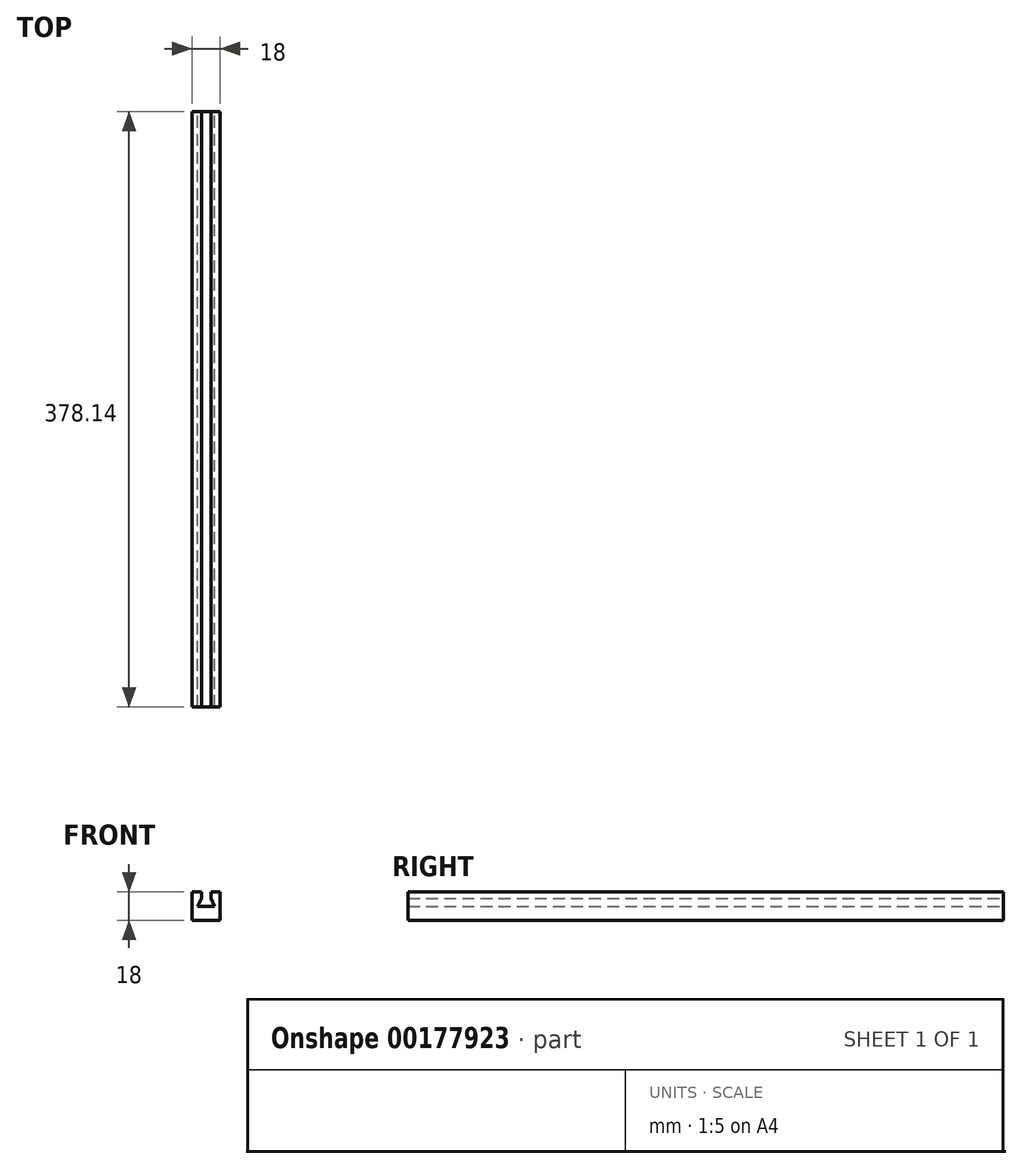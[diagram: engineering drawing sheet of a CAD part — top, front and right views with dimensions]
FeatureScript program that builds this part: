
annotation { "Feature Type Name" : "Feature", "Feature Type Description" : "" }
export const myFeature = defineFeature(function(context is Context, id is Id, definition is map)
    precondition{}
    {
        {
            var Q0;
            Q0=qCreatedBy(makeId("Front.planeOp"),FACE);
            var sketch = newSketch(context, id + "F0", { "sketchPlane" : qUnion([Q0])});
            skLineSegment(sketch, "E0.trimOffspring", {"start": v(3, 6.57) * mm, "end": v(9, 6.57) * mm});
            skLineSegment(sketch, "E1", {"start": v(3, 2.57) * mm, "end": v(3, 6.57) * mm});
            skLineSegment(sketch, "E2", {"start": v(9, 6.57) * mm, "end": v(9, -11.43) * mm});
            skLineSegment(sketch, "E3", {"start": v(3, 2.57) * mm, "end": v(5.3, -2.66) * mm});
            skLineSegment(sketch, "E4", {"start": v(5.3, -2.66) * mm, "end": v(0, -2.66) * mm});
            skLineSegment(sketch, "E5", {"start": v(9, -11.43) * mm, "end": v(0, -11.43) * mm});
            skLineSegment(sketch, "E6.MirrorCS", {"start": v(-3, 6.57) * mm, "end": v(-9, 6.57) * mm});
            skLineSegment(sketch, "E7.MirrorCS", {"start": v(-9, -11.43) * mm, "end": v(0, -11.43) * mm});
            skLineSegment(sketch, "E8.MirrorCS", {"start": v(-5.3, -2.66) * mm, "end": v(0, -2.66) * mm});
            skLineSegment(sketch, "E9.MirrorCS", {"start": v(-3, 2.57) * mm, "end": v(-3, 6.57) * mm});
            skLineSegment(sketch, "E10.MirrorCS", {"start": v(-9, 6.57) * mm, "end": v(-9, -11.43) * mm});
            skLineSegment(sketch, "E11.MirrorCS", {"start": v(-3, 2.57) * mm, "end": v(-5.3, -2.66) * mm});
            skSolve(sketch);
        }
        {
            var Q0;
            Q0 = qSketchRegion(id + "F0", true);
            extrude(context, id + "F1", {"entities" : qUnion([Q0]), "endBound" : BoundingType.SYMMETRIC, "depth" : (378.15) * mm});
        }
    });
